FCSTD DOCUMENT  (FreeCAD 0.16RUnknown)
Label: h1
License: All rights reserved
LicenseURL: http://en.wikipedia.org/wiki/All_rights_reserved
objects: Part::FeaturePython×2, Spreadsheet::Sheet×1, Sketcher::SketchObject×1, Part::Part2DObjectPython×1
note: 4 computed .brp shape members not serialized (recipe doc carries the construction recipe); baked Part::Feature solids carry a one-line shape summary decoded from their .brp

FEATURE [Spreadsheet::Sheet] Spreadsheet  label="param"
  cells = A1=radius; B1(radius)=0.5; C1=mm; A2=factor; B2(factor)=3; A3=replicate; B3(replicate)==param.big / param.radius * param.factor / 4; A4=big; B4(big)=75; C4=mm; A5=distance; B5(distance)=0.5; A6=hdistance; B6(hdistance)==radius * cos(30) * 2 + distance; A7=vdistance; B7(vdistance)==sqrt(param.hdistance * param.hdistance * 3 / 4); A8=hreplicate; B8(hreplicate)==param.big * 2 / param.hdistance + 1; A9=vreplicate; B9(vreplicate)==param.big / param.vdistance + 2
FEATURE [Sketcher::SketchObject] Sketch  label="hexagon"
  expr: Constraints[12] = param.radius
  sketch-geometry (6):
    g0: LineSegment StartX=8.98433 StartY=-1.50369 StartZ=0 EndX=8.98433 EndY=-2.00369 EndZ=0
    g1: LineSegment StartX=8.98433 StartY=-2.00369 StartZ=0 EndX=9.41735 EndY=-2.25369 EndZ=0
    g2: LineSegment StartX=9.41735 StartY=-2.25369 StartZ=0 EndX=9.85036 EndY=-2.00369 EndZ=0
    g3: LineSegment StartX=9.85036 StartY=-2.00369 StartZ=0 EndX=9.85036 EndY=-1.50369 EndZ=0
    g4: LineSegment StartX=9.85036 StartY=-1.50369 StartZ=0 EndX=9.41735 EndY=-1.25369 EndZ=0
    g5: LineSegment StartX=9.41735 StartY=-1.25369 StartZ=0 EndX=8.98433 EndY=-1.50369 EndZ=0
  constraints (18):
    c: Coincident(g0,g1)
    c: Coincident(g1,g2)
    c: Coincident(g2,g3)
    c: Vertical(g3)
    c: Coincident(g3,g4)
    c: Coincident(g4,g5)
    c: Coincident(g5,g0)
    c: Angle(g5,g4) = 2.0944
    c: Angle(g4,g3) = 2.0944
    c: Angle(g3,g2) = 2.0944
    c: Angle(g2,g1) = 2.0944
    c: Angle(g1,g0) = 2.0944
    c: Distance(g5) = 0.5
    c: Equal(g5,g0)
    c: Equal(g5,g4)
    c: Equal(g4,g3)
    c: Equal(g2,g1)
    c: Equal(g0,g1)
FEATURE [Part::FeaturePython] Array002  # Draft array (typed FeaturePython)
  Angle = 360
  ArrayType = 0
  Axis = (0,0,1)
  Base = -> Sketch
  Center = (0,0,0)
  Fuse = false
  IntervalAxis = (0,0,0)
  IntervalX = (1.36603,0,0)
  IntervalY = (0.683013,1.18301,0)
  IntervalZ = (0,0,0)
  NumberPolar = 1
  NumberX = 111
  NumberY = 2
  NumberZ = 1
  expr: IntervalY.x = param.hdistance / 2
  expr: IntervalX.x = param.hdistance
  expr: IntervalY.y = param.vdistance
  expr: NumberX = param.hreplicate
FEATURE [Part::FeaturePython] Array003  label="holesHexagon"  # Draft array (typed FeaturePython)
  Angle = 360
  ArrayType = 0
  Axis = (0,0,1)
  Base = -> Array002
  Center = (0,0,0)
  Fuse = false
  IntervalAxis = (0,0,0)
  IntervalX = (1,0,0)
  IntervalY = (0,2.36603,0)
  IntervalZ = (0,0,0)
  NumberPolar = 1
  NumberX = 1
  NumberY = 65
  NumberZ = 1
  expr: IntervalY.y = param.vdistance * 2
  expr: NumberY = param.vreplicate
FEATURE [Part::Part2DObjectPython] Circle002  label="big001"  # Draft 2D object (typed FeaturePython)
  FirstAngle = 0
  LastAngle = 0
  MakeFace = true
  Placement = pos=(84.375,75,0) rot=(0,0,1;0rad)
  Radius = 75
  expr: Placement.Base.y = param.big
  expr: Placement.Base.x = param.radius * param.factor * param.replicate / 2
  expr: Radius = param.big
